# Revit family: Alma-KMDUAL16-Cleo Pull Down Dual Spray Mixer-Nickel
name_source: partatom
category: Plumbing Fixtures
units: mm (PartAtom-declared; Revit-internal decimal feet)

## family parameters
Always vertical = Yes
Cut with Voids When Loaded = No
Maintain Annotation Orientation = No
OmniClass Number = 23.45.00.00
OmniClass Title = Sanitary, Laundry, and Cleaning Equipment
Part Type = Normal
Room Calculation Point = No
Round Connector Dimension = Use Diameter
Shared = No
Work Plane-Based = No

## types (1)
- Cleo Nickel
    Brand = Alma
    Default Elevation = 0 mm  [stored 0 ft]
    Description = Cleo Pull Down Dual Spray Mixer
    Handle Material = Alma Black
    Hose Material = Alma Black
    Manufacturer = BUILDMAT
    Model = KMDUAL16
    Spring Material = Alma Nickel
    Tap Material = Alma Nickel
    URL = https://www.buildmat.com.au

note: [stored X ft] marks values corroborated as IEEE doubles in the binary element streams (Revit-internal decimal feet)

## geometry (parser evidence)
native form markers: Sweep x3
no freeform markers — native parametric forms only
